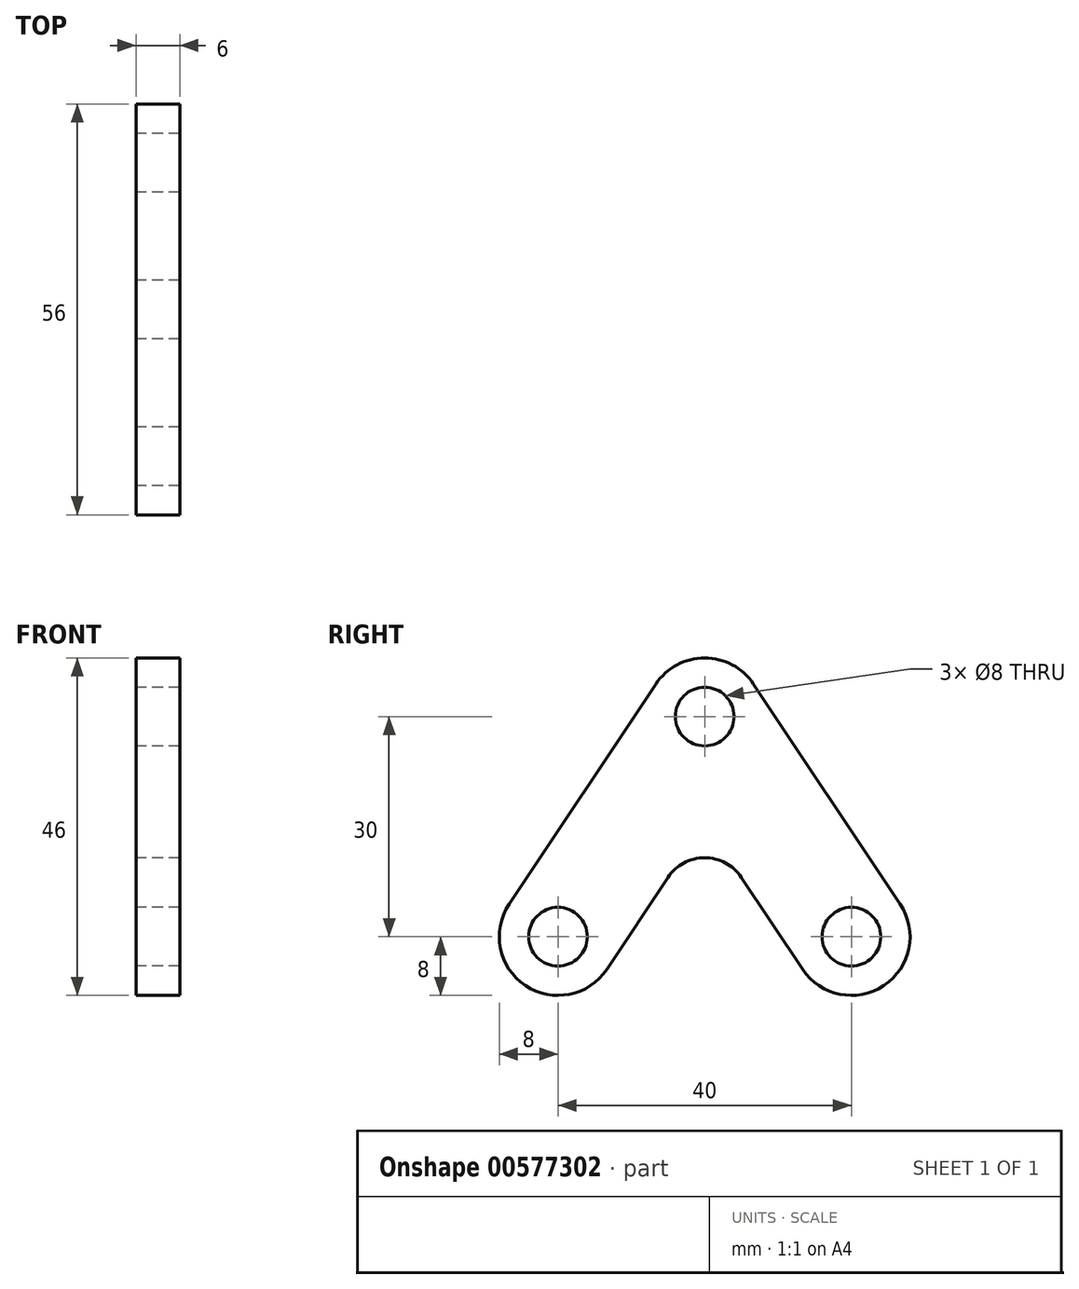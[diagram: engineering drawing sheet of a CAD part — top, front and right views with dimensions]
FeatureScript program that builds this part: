
annotation { "Feature Type Name" : "Feature", "Feature Type Description" : "" }
export const myFeature = defineFeature(function(context is Context, id is Id, definition is map)
    precondition{}
    {
        {
            var Q0;
            Q0=qCreatedBy(makeId("Right.planeOp"),FACE);
            var sketch = newSketch(context, id + "F0", { "sketchPlane" : qUnion([Q0])});
            skArc(sketch, "E0", {"start": v(6.66, 4.44) * mm, "mid": v(0, 8) * mm, "end": v(-6.66, 4.44) * mm});
            skArc(sketch, "E1", {"start": v(13.34, -34.44) * mm, "mid": v(24.44, -36.66) * mm, "end": v(26.66, -25.56) * mm});
            skArc(sketch, "E2", {"start": v(-26.66, -25.56) * mm, "mid": v(-24.44, -36.66) * mm, "end": v(-13.34, -34.44) * mm});
            skLineSegment(sketch, "E3", {"start": v(13.34, -34.44) * mm, "end": v(5, -21.91) * mm});
            skLineSegment(sketch, "E4", {"start": v(-5, -21.91) * mm, "end": v(-13.34, -34.44) * mm});
            skLineSegment(sketch, "E5", {"start": v(26.66, -25.56) * mm, "end": v(6.66, 4.44) * mm});
            skLineSegment(sketch, "E6", {"start": v(-6.66, 4.44) * mm, "end": v(-26.66, -25.56) * mm});
            skCircle(sketch, "E7", {"center": v(20, -30) * mm, "radius": 4 * mm});
            skCircle(sketch, "E8", {"center": v(0, 0) * mm, "radius": 4 * mm});
            skCircle(sketch, "E9", {"center": v(-20, -30) * mm, "radius": 4 * mm});
            skPoint(sketch, "E10.visualSharp", {"position": v(0, -14.42) * mm});
            skArc(sketch, "E10.filletArc", {"start": v(5, -21.91) * mm, "mid": v(0, -19.24) * mm, "end": v(-5, -21.91) * mm});
            skSolve(sketch);
        }
        {
            var Q0;
            Q0 = qSketchRegion(id + "F0", true);
            extrude(context, id + "F1", {"entities" : qUnion([Q0]), "depth" : 6 * mm, "offsetDistance" : 25 * mm});
        }
    });
